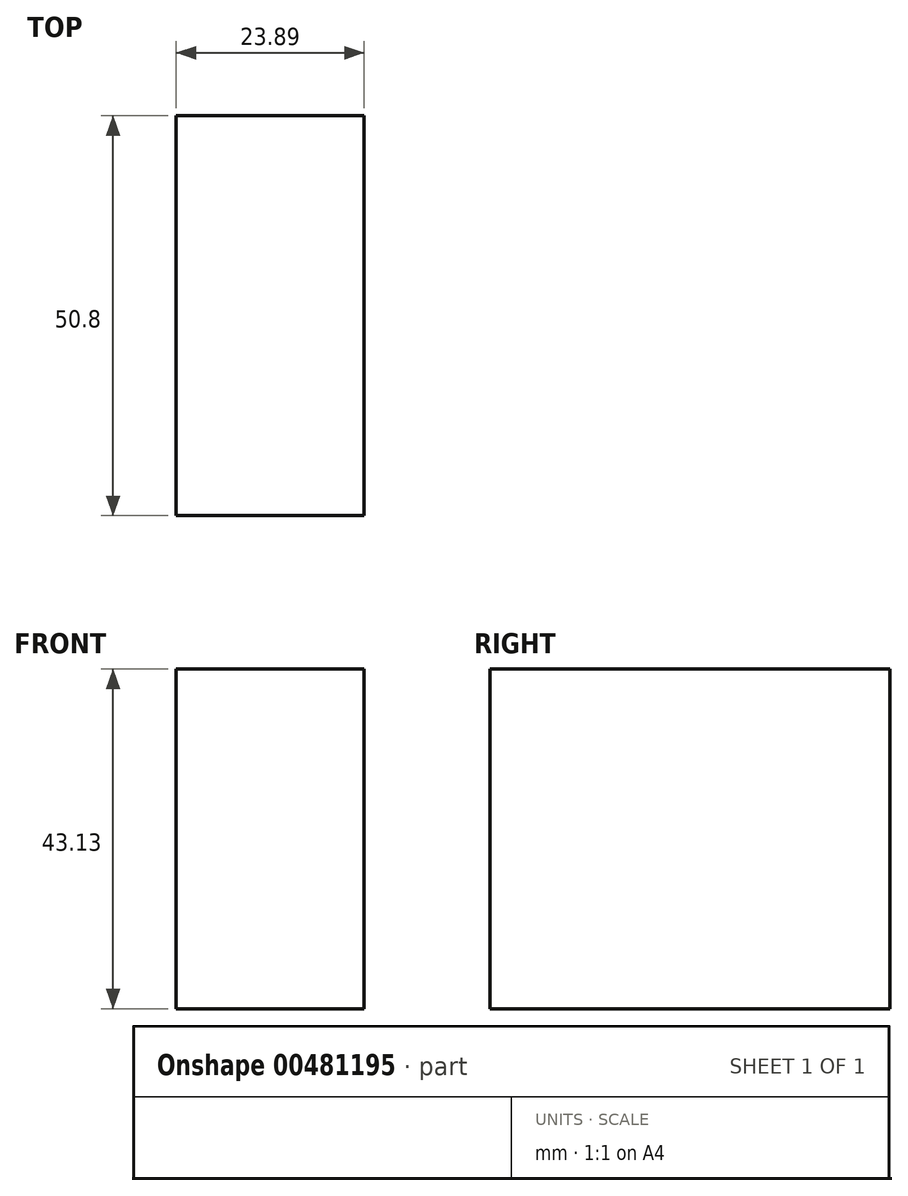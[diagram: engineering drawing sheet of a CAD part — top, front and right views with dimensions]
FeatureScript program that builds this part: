
annotation { "Feature Type Name" : "Feature", "Feature Type Description" : "" }
export const myFeature = defineFeature(function(context is Context, id is Id, definition is map)
    precondition{}
    {
        {
            var Q0;
            Q0=qCreatedBy(makeId("Front.planeOp"),FACE);
            var sketch = newSketch(context, id + "F0", { "sketchPlane" : qUnion([Q0])});
            skLineSegment(sketch, "E0.bottom", {"start": v(-11.23, -3.85) * mm, "end": v(-35.12, -3.85) * mm});
            skLineSegment(sketch, "E0.top", {"start": v(-11.23, 39.28) * mm, "end": v(-35.12, 39.28) * mm});
            skLineSegment(sketch, "E0.left", {"start": v(-11.23, -3.85) * mm, "end": v(-11.23, 39.28) * mm});
            skLineSegment(sketch, "E0.right", {"start": v(-35.12, -3.85) * mm, "end": v(-35.12, 39.28) * mm});
            skSolve(sketch);
        }
        {
            var Q0;
            Q0=makeQuery(id+"F0.imprint","IMPRINT",FACE,{"disambiguationData":[TD([[makeQuery(id+"F0.imprint","IMPRINT",EDGE,{"derivedFrom":sQuery(id+"F0.wireOp",EDGE,"E0.bottom")}),-1.0]])]});
            extrude(context, id + "F1", {"entities" : qUnion([Q0]), "depth" : 50.8 * mm});
        }
    });
